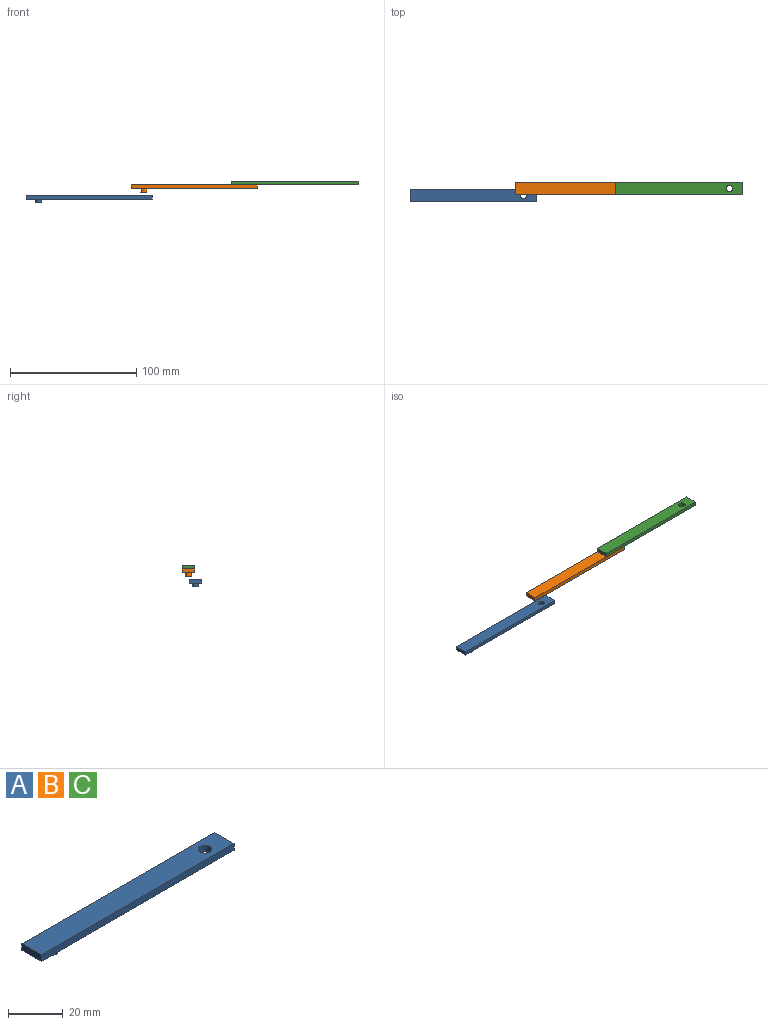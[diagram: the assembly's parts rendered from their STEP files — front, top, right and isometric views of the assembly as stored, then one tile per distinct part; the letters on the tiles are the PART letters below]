
ASSEMBLY  parts=3 mates=1
PART A: 9 faces, bbox 100x10x6 mm
  f0: plane 10x3mm, normal (1,0,0), area 30mm2, adj f1,f3,f5,f6
  f1: plane 100x3mm, normal (0,1,0), area 300mm2, adj f0,f2,f5,f6
  f2: plane 10x3mm, normal (-1,0,0), area 30mm2, adj f1,f3,f5,f6
  f3: plane 100x3mm, normal (0,-1,0), area 300mm2, adj f0,f2,f5,f6
  f4: cylinder r=2.5mm len=5mm, axis (0,0,-1), area 47.1mm2, adj f5,f6
  f5: plane 100x10mm, normal (0,0,1), area 980.4mm2, adj f0,f1,f2,f3,f4
  f6: plane 100x10mm, normal (0,0,-1), area 960.7mm2, adj f0,f1,f2,f3,f4,f7
  f7: cylinder r=2.5mm len=5mm, axis (0,0,1), area 47.1mm2, adj f6,f8
  f8: plane 5x5mm, normal (0,0,-1), area 19.6mm2, adj f7
PART B: same geometry as A
PART C: same geometry as A
PLACE A t=(-78.24,-2.03,-7.56)mm
PLACE B t=(5.16,3.4,0.64)mm
PLACE C t=(85.16,3.4,3.64)mm
MATE revolute C.f7 <-> B.f4  axis (0,0,-1) through (45.16,3.4,0.64)mm
